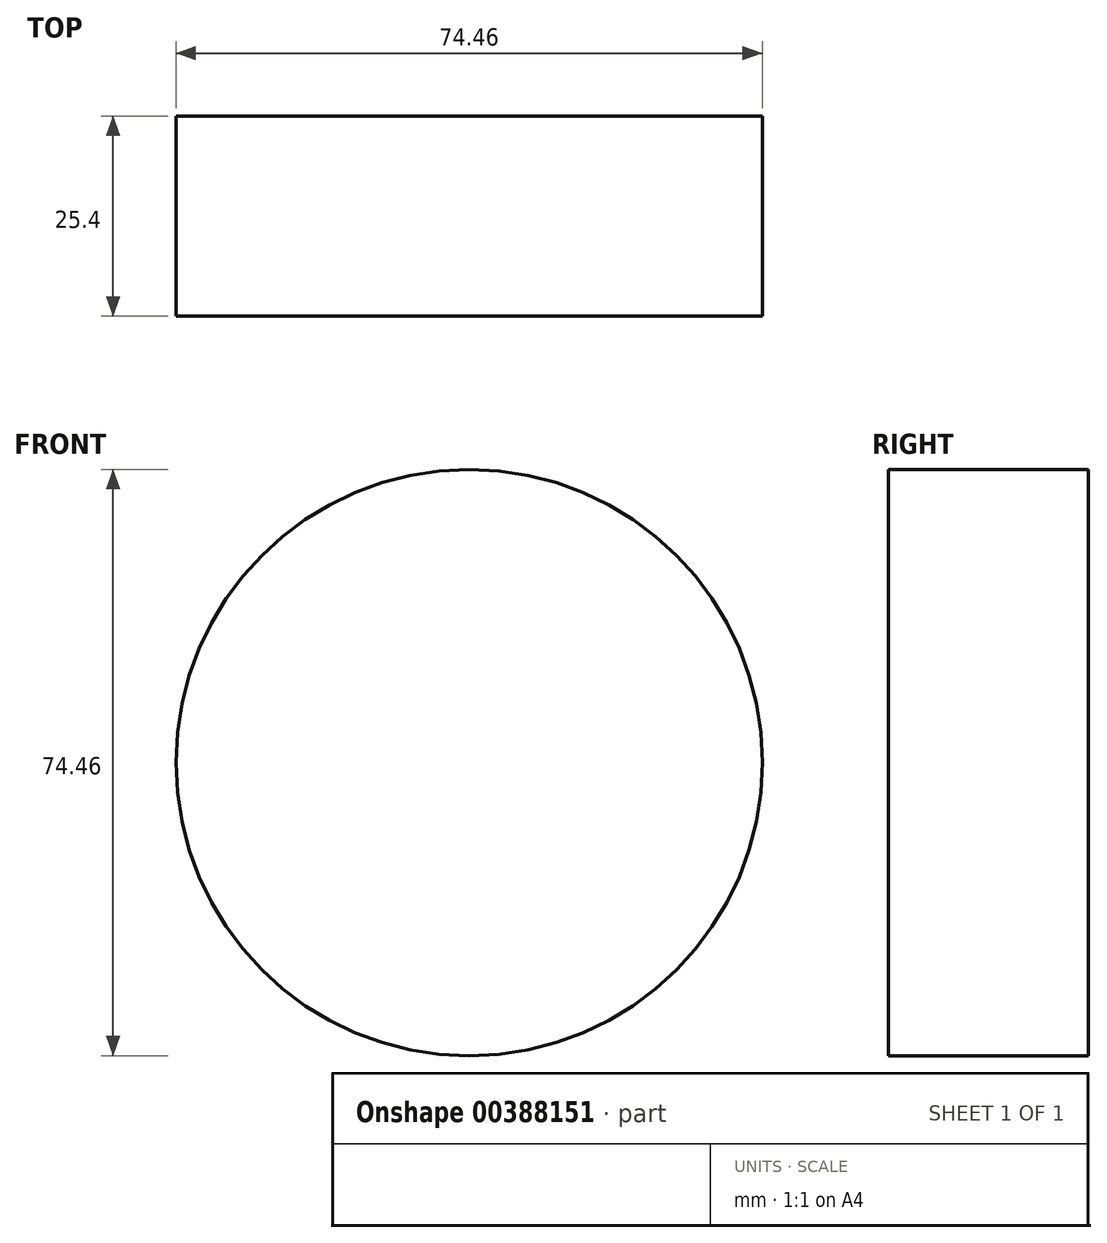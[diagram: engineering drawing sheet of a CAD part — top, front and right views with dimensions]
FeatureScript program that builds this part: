
annotation { "Feature Type Name" : "Feature", "Feature Type Description" : "" }
export const myFeature = defineFeature(function(context is Context, id is Id, definition is map)
    precondition{}
    {
        {
            var Q0;
            Q0=qCreatedBy(makeId("Front.planeOp"),FACE);
            var sketch = newSketch(context, id + "F0", { "sketchPlane" : qUnion([Q0])});
            skCircle(sketch, "E0", {"center": v(0, 0) * mm, "radius": 37.23 * mm});
            skSolve(sketch);
        }
        {
            var Q0;
            Q0 = qSketchRegion(id + "F0", true);
            extrude(context, id + "F1", {"entities" : qUnion([Q0]), "depth" : 25.4 * mm});
        }
    });
